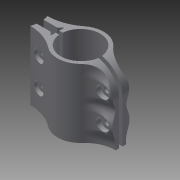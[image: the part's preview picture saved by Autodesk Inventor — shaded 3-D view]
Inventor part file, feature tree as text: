
AUTODESK INVENTOR PART (.ipt)
format: ipt  version: 2015 (Build 190159000, 159)  size: 627,712 bytes
history: native  units: in
note: dims shown in document units (in); Inventor stores cm internally (conversion verified against a paired STEP export)
features: extrude x8, sketch x7, fillet x3, mirror x2, plane x1
ambient origin geometry x8: Origin, YZ Plane, XZ Plane, XY Plane, X Axis, Y Axis, Z Axis, Center Point
bodies: Solid1 (feature_tree)
feature tree (21):
  extrude  "Extrusion1"  Depth=1.35in
  extrude  "Extrusion2"  Depth=0.5in
  extrude  "Extrusion3"  Depth=0.3in
  extrude  "Extrusion4"  Depth=0.5in
  extrude  "Extrusion5"  Depth=0.2in
  plane  "Work Plane1"
  extrude  "Extrusion6"  Depth=0.05in
  mirror  "Mirror1"
  extrude  "Extrusion7"  Depth=2.0in TaperAngle=0.0deg
  extrude  "Extrusion8"  Depth=0.18in
  mirror  "Mirror2"
  fillet  "Fillet1"  Radius=0.18in
  fillet  "Fillet2"  Radius=0.25in
  fillet  "Fillet3"  Radius=0.25in
  sketch  "Sketch1"  dims[d0=1.15in d1=1.35in]
  sketch  "Sketch2"  dims[d2=2.0in d3=0.0in d5=0.5in]
  sketch  "Sketch3"  dims[d6=0.15in d7=0.3in]
  sketch  "Sketch4"  dims[d8=2.0in d9=0.0in d10=0.5in]
  sketch  "Sketch6"  dims[d11=1.5in d13=0.2in]
  sketch  "Sketch7"  dims[d17=2.0in d18=0.0in d19=0.05in]
  sketch  "Sketch8"  dims[d20=0.1in d21=2.0in d22=0.0in d23=0.18in d24=0.18in d25=0.25in d26=0.25in d29=2.0in d30=0.0in d31=0.25in d32=0.36in d33=0.36in d34=2.0in d35=0.0in d36=0.4in d37=0.4in d38=0.15in d39=0.0in d40=0.02in d41=0.0in d42=0.36in d43=0.12in d44=0.0in d45=0.36in d46=0.6in d47=0.5in d48=0.5in d49=0.75in d50=0.3in d51=0.09in d52=0.0in]
